# Revit family: LOROWERK 21512-070X
name_source: partatom
category: Plumbing Fixtures
revit_build: Autodesk Revit 2017 (Build: 20160225_1515(x64)
units: mm (PartAtom-declared; Revit-internal decimal feet)

## family parameters
Always vertical = Yes
Cut with Voids When Loaded = No
Part Type = Normal
Room Calculation Point = No
Round Connector Dimension = Use Diameter
Shared = No
Work Plane-Based = No

## types (1)
- LOROWERK 21512-070X
    Abdichtvarianten = mit Klemmflansch (Pressdichtungsflansch)
    Abflussstutzen Ausführung = senkrecht
    Ablaufanschluss = mittig
    Anschluss an GLT, GA = No
    BIM = https://media.stage.bim.site
    CONNECTOR0_DIAMETER_dZ_0r = 70 mm
    CONNECTOR0_dZ_00 = 12 mm  [stored 0.0393701 ft]
    CONNECTOR0_dZ_01 = 13 mm
    CONNECTOR0_ref_dZ = 13 mm
    CONNECTOR1_DIAMETER_dZ_0r = 70 mm
    CONNECTOR1_dZ_00 = 260 mm
    CONNECTOR1_dZ_01 = 23 mm
    CONNECTOR1_ref_dZ = 23 mm
    DATANORM = 21512.070X
    Description = LORO-DRAINLET DL Flachdachabläufe, Kompletteinheiten, einteilig
    Einbaubreite [m] = 0.26
    Einbauhöhe [m] = 0.376
    Einbautiefe [m] = 0.26
    Elektrischer Anschluss = No
    Feuerwiderstandsklasse nachrüstbar 7 = No
    GTIN = 4038088073421
    Gehäuseanschlussarten = Ablauf-Punktförmig
    Geruchsverschluss = ohne Geruchverschluss
    HAN = 21512.070X
    Ist System = No
    Ist Zubehör = No
    Komplettartikel (Einteilig) aus Kombination (Mehrteileausführung) Ablaufgrundkörper und Aufsatzstück = Yes
    Manufacturer = LOROWERK K.H. Vahlbrauk GmbH & Co. KG
    Nenndrucksystem = PN
    Nennmaß = 70
    Nennweitensystem = DN
    Potenzialausgleich (Erdungsanschluss) vorhanden = No
    Produktbezeichnung = LORO-DRAINLET DL Flachdachabläufe, Kompletteinheiten, einteilig
    Produktklassifikation = Flachdachablauf
    Produktname = LORO-DL Ablauf, Edelstahl, Klemmflansch, senkr., 1-tlg., mit WD, DN70
    Produktvideo = https://media.stage.bim.site
    Sperrwasserhöhe [m] = 0.035
    Typ = Dachablauf
    Type Name = LORO-DL Ablauf, Edelstahl, Klemmflansch, senkr., 1-tlg., mit WD, DN70
    VDIBSN = 0020030000010010000010010010010000000030020000000600000001
    Variante/Varianten-Art/Zubehörbezeichnung = ohne Begleitheizung
    Werkstoff des Ablaufkörpers = nicht rostender Stahl
    mit Blätter-/Kiesfang = Yes
    mit Schallentkopplung = No

note: [stored X ft] marks values corroborated as IEEE doubles in the binary element streams (Revit-internal decimal feet)

## geometry (parser evidence)
native form markers: Blend x2, Sweep x2
no freeform markers — native parametric forms only
